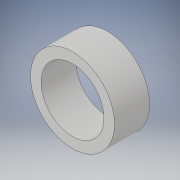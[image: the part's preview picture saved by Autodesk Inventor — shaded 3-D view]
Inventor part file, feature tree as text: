
AUTODESK INVENTOR PART (.ipt)
format: ipt  version: 2019 (Build 230136000, 136)  size: 102,912 bytes
history: native  units: mm
features: extrude x2, sketch x2
ambient origin geometry x8: Origin, YZ Plane, XZ Plane, XY Plane, X Axis, Y Axis, Z Axis, Center Point
bodies: Solid1 (feature_tree)
feature tree (4):
  extrude  "Extrusion1"  Depth=100.0mm TaperAngle=0.0deg
  extrude  "Extrusion2"  Depth=10.0mm TaperAngle=0.0deg
  sketch  "Sketch1"  dims[d0=240.0mm d1=100.0mm d2=0.0mm]
  sketch  "Sketch2"  dims[d3=180.0mm d4=10.0mm d5=0.0mm]
